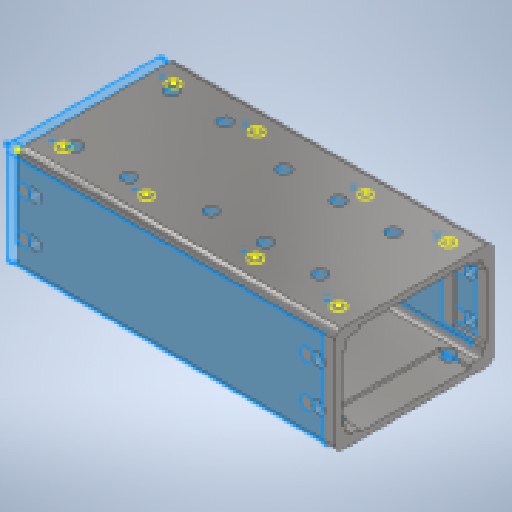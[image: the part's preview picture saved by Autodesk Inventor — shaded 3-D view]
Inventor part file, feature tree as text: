
AUTODESK INVENTOR PART (.ipt)
format: ipt  version: 2025.2 (Build 292293000, 293)  size: 284,160 bytes
history: native  units: in
note: dims shown in document units (in); Inventor stores cm internally (conversion verified against a paired STEP export)
features: extrude x6, mirror x2, sketch x2, projected_geometry x2, shell x1, fillet x1, plane x1
ambient origin geometry x8: Origin, YZ Plane, XZ Plane, XY Plane, X Axis, Y Axis, Z Axis, Center Point
bodies: Solid1 (feature_tree)
feature tree (15):
  extrude  "Extrusion1"  Depth=2.0in
  shell  "Shell1"  Thickness=6.0in
  fillet  "Fillet1"  Radius=0.1875in
  plane  "Work Plane1"
  extrude  "Extrusion2"  Depth=0.5768in
  mirror  "Mirror1"
  extrude  "Extrusion3"  Depth=2.0866in
  extrude  "Extrusion4"  Depth=0.5768in
  extrude  "Extrusion5"  Depth=0.3937in
  mirror  "Mirror2"
  extrude  "Extrusion6"  Depth=6.0in TaperAngle=0.0deg
  sketch  "Sketch8"  dims[d5=0.125in d6=0.2362in d7=2.0866in d8=1.5748in d9=0.3937in d10=6.0in d11=0.0in d12=0.25in d13=2.0in d14=3.0in d16=0.5906in d17=0.4921in d18=1.0in d19=0.0in d20=4.0in d21=3.0in d22=2.0in d23=2.5in d24=0.25in d25=0.25in d27=0.5906in d28=1.0in d29=0.0in d31=3.5in d32=2.0in d33=0.6299in d34=0.25in d35=0.7874in d36=0.0in d37=0.0in d38=1.0in d39=2.75in d40=1.75in d41=1.5in d42=1.2126in d43=2.0866in d44=0.5768in d45=0.0in d46=1.378in]
  sketch  "Sketch7"  dims[d0=3.0in d1=2.0in d2=6.0in d3=0.0in d4=0.1875in]
  projected_geometry  "Projected Loop1"
  projected_geometry  "Projected Loop2"
